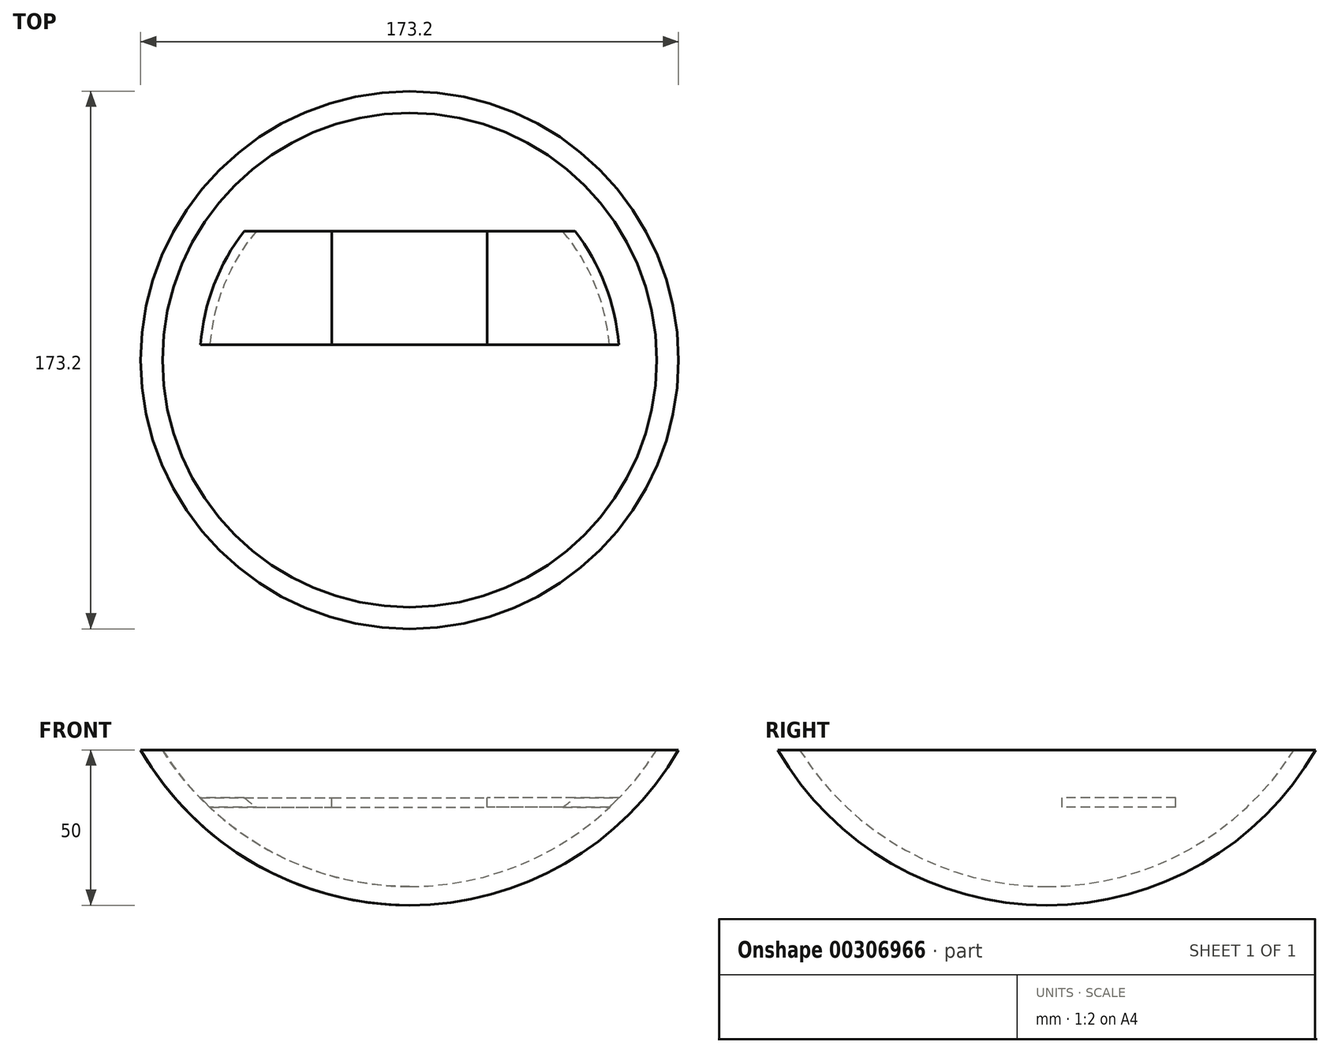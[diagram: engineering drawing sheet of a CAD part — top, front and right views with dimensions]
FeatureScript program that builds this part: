
annotation { "Feature Type Name" : "Feature", "Feature Type Description" : "" }
export const myFeature = defineFeature(function(context is Context, id is Id, definition is map)
    precondition{}
    {
        {
            var Q0;
            Q0=qCreatedBy(makeId("Front.planeOp"),FACE);
            var sketch = newSketch(context, id + "F0", { "sketchPlane" : qUnion([Q0])});
            skArc(sketch, "E0", {"start": v(-86.6, -50) * mm, "mid": v(-50, -86.6) * mm, "end": v(0, -100) * mm});
            skLineSegment(sketch, "E1", {"start": v(0, -50) * mm, "end": v(0, -100) * mm});
            skLineSegment(sketch, "E2", {"start": v(0, -50) * mm, "end": v(-86.6, -50) * mm});
            skPoint(sketch, "E3.orphan", {"position": v(0, 100) * mm});
            skSolve(sketch);
        }
        {
            var Q0;
            Q0=makeQuery(id+"F0.imprint","IMPRINT",FACE,{"disambiguationData":[TD([[makeQuery(id+"F0.imprint","IMPRINT",EDGE,{"derivedFrom":sQuery(id+"F0.wireOp",EDGE,"E0")}),1.0]])]});
            var Q1;
            Q1=sQuery(id+"F0.wireOp",EDGE,"E1");
            revolve(context, id + "F1", {"entities" : qUnion([Q0]), "axis" : qUnion([Q1]), "revolveType" : RevolveType.FULL});
        }
        {
            var Q0;
            Q0=makeQuery(id+"F1.opRevolve","SWEPT_FACE",FACE,{"disambiguationData":[OSD([sQuery(id+"F0.wireOp",EDGE,"E2")])]});
            shell(context, id + "F2", {"entities" : qUnion([Q0]), "thickness" : 6 * mm});
        }
        {
            var Q0;
            Q0=qCreatedBy(makeId("Front.planeOp"),FACE);
            cPlane(context, id + "F3", {"entities" : qUnion([Q0]), "cplaneType" : CPlaneType.OFFSET, "offset" : 5 * mm, "oppositeDirection" : true, "width" : 150 * mm, "height" : 150 * mm});
        }
        {
            var Q0;
            Q0=qCreatedBy(id+"F3.planeOp",FACE);
            var sketch = newSketch(context, id + "F4", { "sketchPlane" : qUnion([Q0])});
            skLineSegment(sketch, "E4.bottom", {"start": v(-25, -68.4) * mm, "end": v(25, -68.4) * mm});
            skLineSegment(sketch, "E4.top", {"start": v(-25, -65.4) * mm, "end": v(25, -65.4) * mm});
            skLineSegment(sketch, "E4.left", {"start": v(-25, -68.4) * mm, "end": v(-25, -65.4) * mm});
            skLineSegment(sketch, "E4.right", {"start": v(25, -68.4) * mm, "end": v(25, -65.4) * mm});
            skSolve(sketch);
        }
        {
            var Q0;
            Q0 = qSketchRegion(id + "F4", true);
            extrude(context, id + "F5", {"entities" : qUnion([Q0]), "oppositeDirection" : true, "depth" : 36.5 * mm});
        }
        {
            var Q0;
            Q0=makeQuery(id+"F5.opExtrude","SWEPT_FACE",FACE,{"disambiguationData":[OSD([sQuery(id+"F4.wireOp",EDGE,"E4.right")])]});
            extrude(context, id + "F6", {"entities" : qUnion([Q0]), "endBound" : BoundingType.UP_TO_NEXT, "depth" : 25 * mm});
        }
        {
            var Q0;
            Q0=makeQuery(id+"F5.opExtrude","SWEPT_FACE",FACE,{"disambiguationData":[OSD([sQuery(id+"F4.wireOp",EDGE,"E4.left")])]});
            extrude(context, id + "F7", {"entities" : qUnion([Q0]), "endBound" : BoundingType.UP_TO_NEXT, "depth" : 25 * mm});
        }
    });
